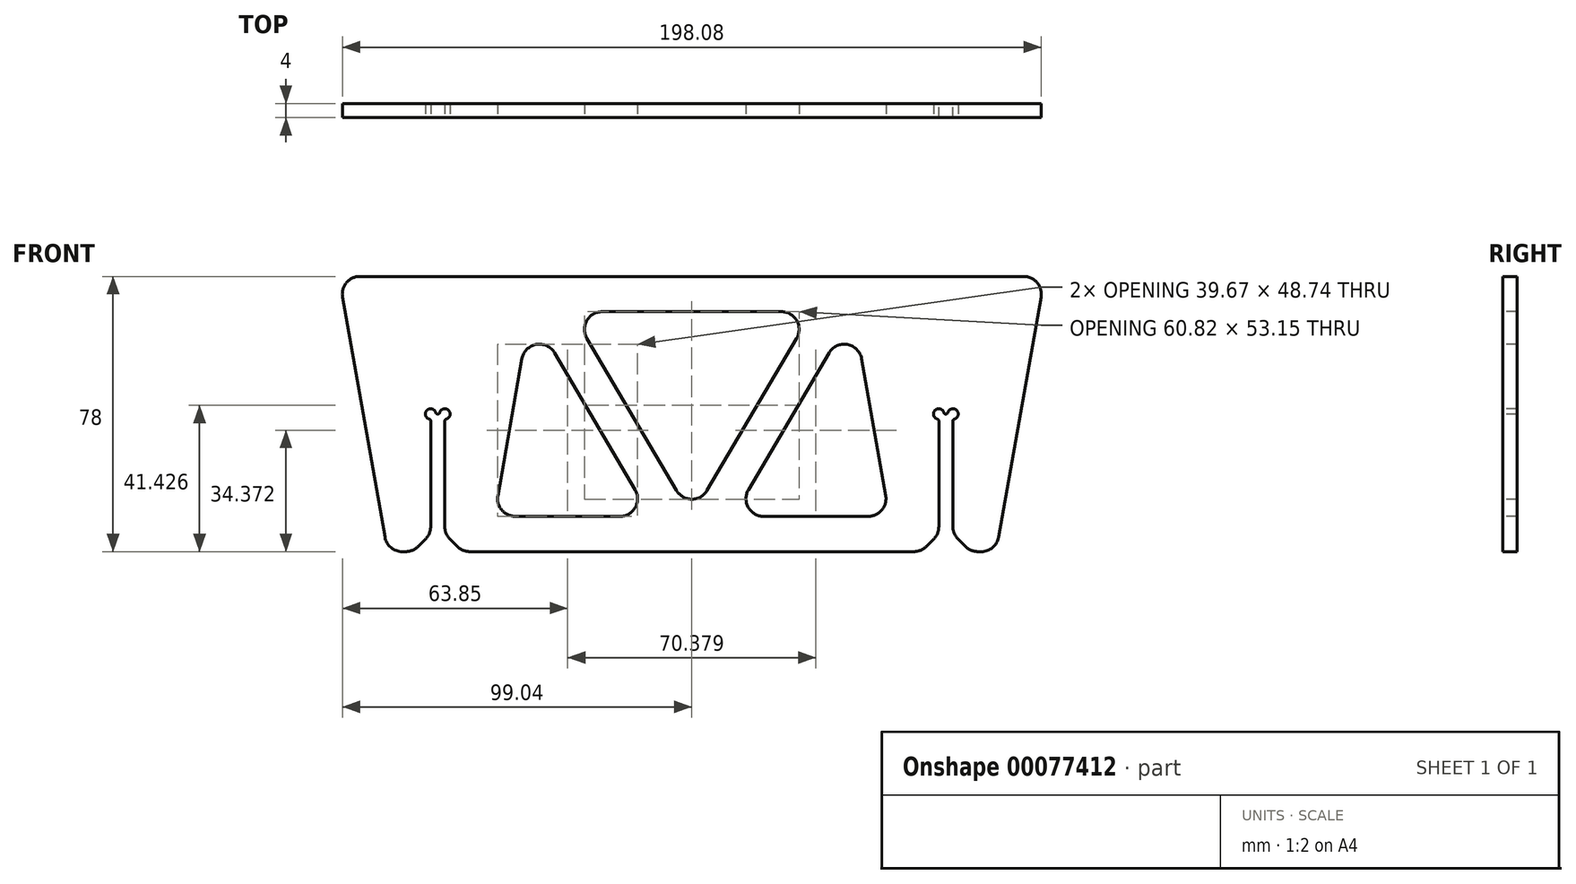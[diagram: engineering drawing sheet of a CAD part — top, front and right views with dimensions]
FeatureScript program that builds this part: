
annotation { "Feature Type Name" : "Feature", "Feature Type Description" : "" }
export const myFeature = defineFeature(function(context is Context, id is Id, definition is map)
    precondition{}
    {
        {
            var Q0;
            Q0=qCreatedBy(makeId("Front.planeOp"),FACE);
            var sketch = newSketch(context, id + "F0", { "sketchPlane" : qUnion([Q0])});
            skLineSegment(sketch, "E0", {"start": v(0, 104.96) * mm, "end": v(0, -105.42) * mm, "construction": true});
            skLineSegment(sketch, "E1", {"start": v(-94.04, 0) * mm, "end": v(94.04, 0) * mm});
            skLineSegment(sketch, "E2", {"start": v(98.97, -5.87) * mm, "end": v(86.98, -73.87) * mm});
            skLineSegment(sketch, "E3", {"start": v(82.05, -78) * mm, "end": v(74, -78) * mm});
            skLineSegment(sketch, "E4", {"start": v(-86.98, -73.87) * mm, "end": v(-98.97, -5.87) * mm});
            skLineSegment(sketch, "E5", {"start": v(-74, -78) * mm, "end": v(-74, -39) * mm});
            skLineSegment(sketch, "E6", {"start": v(-74, -39) * mm, "end": v(-70, -39) * mm});
            skLineSegment(sketch, "E7", {"start": v(-70, -39) * mm, "end": v(-70, -78) * mm});
            skLineSegment(sketch, "E8", {"start": v(74, -78) * mm, "end": v(74, -39) * mm});
            skLineSegment(sketch, "E9", {"start": v(70, -39) * mm, "end": v(74, -39) * mm});
            skLineSegment(sketch, "E10", {"start": v(70, -39) * mm, "end": v(70, -78) * mm});
            skLineSegment(sketch, "E11.trimOffspring", {"start": v(-74, -78) * mm, "end": v(-82.05, -78) * mm});
            skLineSegment(sketch, "E12.trimOffspring", {"start": v(70, -78) * mm, "end": v(-70, -78) * mm});
            skPoint(sketch, "E13.visualSharp", {"position": v(-100, 0) * mm});
            skArc(sketch, "E13.filletArc", {"start": v(-94.04, 0) * mm, "mid": v(-97.87, -1.79) * mm, "end": v(-98.97, -5.87) * mm});
            skPoint(sketch, "E14.visualSharp", {"position": v(-86.25, -78) * mm});
            skArc(sketch, "E14.filletArc", {"start": v(-86.98, -73.87) * mm, "mid": v(-85.26, -76.83) * mm, "end": v(-82.05, -78) * mm});
            skPoint(sketch, "E15.visualSharp", {"position": v(86.25, -78) * mm});
            skArc(sketch, "E15.filletArc", {"start": v(82.05, -78) * mm, "mid": v(85.26, -76.83) * mm, "end": v(86.98, -73.87) * mm});
            skPoint(sketch, "E16.visualSharp", {"position": v(100, 0) * mm});
            skArc(sketch, "E16.filletArc", {"start": v(98.97, -5.87) * mm, "mid": v(97.87, -1.79) * mm, "end": v(94.04, 0) * mm});
            skSolve(sketch);
        }
        {
            var Q0;
            Q0=makeQuery(id+"F0.imprint","IMPRINT",FACE,{"disambiguationData":[TD([[makeQuery(id+"F0.imprint","IMPRINT",EDGE,{"derivedFrom":sQuery(id+"F0.wireOp",EDGE,"E1")}),-1.0]])]});
            extrude(context, id + "F1", {"entities" : qUnion([Q0]), "endBound" : BoundingType.SYMMETRIC, "depth" : 4 * mm});
        }
        {
            var Q0;
            Q0=makeQuery(id+"F1.opExtrude","SWEPT_EDGE",EDGE,{"disambiguationData":[OSD([sQuery(id+"F0.wireOp",EDGE,"E5"),sQuery(id+"F0.wireOp",EDGE,"E11.trimOffspring")])]});
            var Q1;
            Q1=makeQuery(id+"F1.opExtrude","SWEPT_EDGE",EDGE,{"disambiguationData":[OSD([sQuery(id+"F0.wireOp",EDGE,"E7"),sQuery(id+"F0.wireOp",EDGE,"E12.trimOffspring")])]});
            var Q2;
            Q2=makeQuery(id+"F1.opExtrude","SWEPT_EDGE",EDGE,{"disambiguationData":[OSD([sQuery(id+"F0.wireOp",EDGE,"E10"),sQuery(id+"F0.wireOp",EDGE,"E12.trimOffspring")])]});
            var Q3;
            Q3=makeQuery(id+"F1.opExtrude","SWEPT_EDGE",EDGE,{"disambiguationData":[OSD([sQuery(id+"F0.wireOp",EDGE,"E3"),sQuery(id+"F0.wireOp",EDGE,"E8")])]});
            chamfer(context, id + "F2", {"entities" : qUnion([Q0, Q1, Q2, Q3]), "width" : 5 * mm, "tangentPropagation" : true});
        }
        {
            var Q0;
            {var subQ0=sQuery(id+"F0.wireOp",EDGE,"E8");Q0=makeQuery(id+"F2.opChamfer","BLEND_EDGE",EDGE,{"blendedFrom":[makeQuery(id+"F1.opExtrude","SWEPT_EDGE",EDGE,{"disambiguationData":[OSD([sQuery(id+"F0.wireOp",EDGE,"E3"),subQ0])]}),makeQuery(id+"F1.opExtrude","SWEPT_FACE",FACE,{"disambiguationData":[OSD([subQ0])]})],"blendedInto":[makeQuery(id+"F1.opExtrude","SWEPT_FACE",FACE,{"disambiguationData":[OSD([subQ0])]})]});}
            var Q1;
            {var subQ0=sQuery(id+"F0.wireOp",EDGE,"E3");Q1=makeQuery(id+"F2.opChamfer","BLEND_EDGE",EDGE,{"blendedFrom":[makeQuery(id+"F1.opExtrude","SWEPT_EDGE",EDGE,{"disambiguationData":[OSD([subQ0,sQuery(id+"F0.wireOp",EDGE,"E8")])]}),makeQuery(id+"F1.opExtrude","SWEPT_FACE",FACE,{"disambiguationData":[OSD([subQ0])]})],"blendedInto":[makeQuery(id+"F1.opExtrude","SWEPT_FACE",FACE,{"disambiguationData":[OSD([subQ0])]})]});}
            var Q2;
            {var subQ0=sQuery(id+"F0.wireOp",EDGE,"E10");Q2=makeQuery(id+"F2.opChamfer","BLEND_EDGE",EDGE,{"blendedFrom":[makeQuery(id+"F1.opExtrude","SWEPT_EDGE",EDGE,{"disambiguationData":[OSD([subQ0,sQuery(id+"F0.wireOp",EDGE,"E12.trimOffspring")])]}),makeQuery(id+"F1.opExtrude","SWEPT_FACE",FACE,{"disambiguationData":[OSD([subQ0])]})],"blendedInto":[makeQuery(id+"F1.opExtrude","SWEPT_FACE",FACE,{"disambiguationData":[OSD([subQ0])]})]});}
            var Q3;
            {var subQ0=sQuery(id+"F0.wireOp",EDGE,"E12.trimOffspring");Q3=makeQuery(id+"F2.opChamfer","BLEND_EDGE",EDGE,{"blendedFrom":[makeQuery(id+"F1.opExtrude","SWEPT_EDGE",EDGE,{"disambiguationData":[OSD([sQuery(id+"F0.wireOp",EDGE,"E10"),subQ0])]}),makeQuery(id+"F1.opExtrude","SWEPT_FACE",FACE,{"disambiguationData":[OSD([subQ0])]})],"blendedInto":[makeQuery(id+"F1.opExtrude","SWEPT_FACE",FACE,{"disambiguationData":[OSD([subQ0])]})]});}
            var Q4;
            {var subQ0=sQuery(id+"F0.wireOp",EDGE,"E7");Q4=makeQuery(id+"F2.opChamfer","BLEND_EDGE",EDGE,{"blendedFrom":[makeQuery(id+"F1.opExtrude","SWEPT_EDGE",EDGE,{"disambiguationData":[OSD([subQ0,sQuery(id+"F0.wireOp",EDGE,"E12.trimOffspring")])]}),makeQuery(id+"F1.opExtrude","SWEPT_FACE",FACE,{"disambiguationData":[OSD([subQ0])]})],"blendedInto":[makeQuery(id+"F1.opExtrude","SWEPT_FACE",FACE,{"disambiguationData":[OSD([subQ0])]})]});}
            var Q5;
            {var subQ0=sQuery(id+"F0.wireOp",EDGE,"E12.trimOffspring");Q5=makeQuery(id+"F2.opChamfer","BLEND_EDGE",EDGE,{"blendedFrom":[makeQuery(id+"F1.opExtrude","SWEPT_EDGE",EDGE,{"disambiguationData":[OSD([sQuery(id+"F0.wireOp",EDGE,"E7"),subQ0])]}),makeQuery(id+"F1.opExtrude","SWEPT_FACE",FACE,{"disambiguationData":[OSD([subQ0])]})],"blendedInto":[makeQuery(id+"F1.opExtrude","SWEPT_FACE",FACE,{"disambiguationData":[OSD([subQ0])]})]});}
            var Q6;
            {var subQ0=sQuery(id+"F0.wireOp",EDGE,"E5");Q6=makeQuery(id+"F2.opChamfer","BLEND_EDGE",EDGE,{"blendedFrom":[makeQuery(id+"F1.opExtrude","SWEPT_EDGE",EDGE,{"disambiguationData":[OSD([subQ0,sQuery(id+"F0.wireOp",EDGE,"E11.trimOffspring")])]}),makeQuery(id+"F1.opExtrude","SWEPT_FACE",FACE,{"disambiguationData":[OSD([subQ0])]})],"blendedInto":[makeQuery(id+"F1.opExtrude","SWEPT_FACE",FACE,{"disambiguationData":[OSD([subQ0])]})]});}
            var Q7;
            {var subQ0=sQuery(id+"F0.wireOp",EDGE,"E11.trimOffspring");Q7=makeQuery(id+"F2.opChamfer","BLEND_EDGE",EDGE,{"blendedFrom":[makeQuery(id+"F1.opExtrude","SWEPT_EDGE",EDGE,{"disambiguationData":[OSD([sQuery(id+"F0.wireOp",EDGE,"E5"),subQ0])]}),makeQuery(id+"F1.opExtrude","SWEPT_FACE",FACE,{"disambiguationData":[OSD([subQ0])]})],"blendedInto":[makeQuery(id+"F1.opExtrude","SWEPT_FACE",FACE,{"disambiguationData":[OSD([subQ0])]})]});}
            fillet(context, id + "F3", {"entities" : qUnion([Q0, Q1, Q2, Q3, Q4, Q5, Q6, Q7]), "radius" : 5 * mm, "tangentPropagation" : true, "allowEdgeOverflow" : false});
        }
        {
            var Q0;
            Q0=makeQuery(id+"F1.opExtrude","CAP_FACE",FACE,{"disambiguationData":[OSD([sQuery(id+"F0.wireOp",EDGE,"E1"),sQuery(id+"F0.wireOp",EDGE,"E2"),sQuery(id+"F0.wireOp",EDGE,"E3"),sQuery(id+"F0.wireOp",EDGE,"E4"),sQuery(id+"F0.wireOp",EDGE,"E5"),sQuery(id+"F0.wireOp",EDGE,"E6"),sQuery(id+"F0.wireOp",EDGE,"E7"),sQuery(id+"F0.wireOp",EDGE,"E8"),sQuery(id+"F0.wireOp",EDGE,"E9"),sQuery(id+"F0.wireOp",EDGE,"E10"),sQuery(id+"F0.wireOp",EDGE,"E11.trimOffspring"),sQuery(id+"F0.wireOp",EDGE,"E12.trimOffspring"),sQuery(id+"F0.wireOp",EDGE,"E13.filletArc"),sQuery(id+"F0.wireOp",EDGE,"E14.filletArc"),sQuery(id+"F0.wireOp",EDGE,"E15.filletArc"),sQuery(id+"F0.wireOp",EDGE,"E16.filletArc")])],"isStart":false});
            var sketch = newSketch(context, id + "F4", { "sketchPlane" : qUnion([Q0])});
            skCircle(sketch, "E17", {"center": v(74, -39) * mm, "radius": 1.5 * mm});
            skCircle(sketch, "E18", {"center": v(70, -39) * mm, "radius": 1.5 * mm});
            skCircle(sketch, "E19", {"center": v(-70, -39) * mm, "radius": 1.5 * mm});
            skCircle(sketch, "E20", {"center": v(-74, -39) * mm, "radius": 1.5 * mm});
            skSolve(sketch);
        }
        {
            var Q0;
            Q0 = qSketchRegion(id + "F4", true);
            extrude(context, id + "F5", {"entities" : qUnion([Q0]), "operationType" : NewBodyOperationType.REMOVE, "endBound" : BoundingType.THROUGH_ALL, "oppositeDirection" : true, "depth" : 25 * mm});
        }
        {
            var Q0;
            Q0=makeQuery(id+"F5.boolean.opBoolean","INTERSECT",EDGE,{"derivedFrom":[makeQuery(id+"F1.opExtrude","SWEPT_FACE",FACE,{"disambiguationData":[OSD([sQuery(id+"F0.wireOp",EDGE,"E9")])]}),makeQuery(id+"F5.opExtrude","SWEPT_FACE",FACE,{"disambiguationData":[OSD([sQuery(id+"F4.wireOp",EDGE,"E17")])]})]});
            var Q1;
            Q1=makeQuery(id+"F5.boolean.opBoolean","INTERSECT",EDGE,{"derivedFrom":[makeQuery(id+"F1.opExtrude","SWEPT_FACE",FACE,{"disambiguationData":[OSD([sQuery(id+"F0.wireOp",EDGE,"E8")])]}),makeQuery(id+"F5.opExtrude","SWEPT_FACE",FACE,{"disambiguationData":[OSD([sQuery(id+"F4.wireOp",EDGE,"E17")])]})]});
            var Q2;
            Q2=makeQuery(id+"F5.boolean.opBoolean","INTERSECT",EDGE,{"derivedFrom":[makeQuery(id+"F1.opExtrude","SWEPT_FACE",FACE,{"disambiguationData":[OSD([sQuery(id+"F0.wireOp",EDGE,"E9")])]}),makeQuery(id+"F5.opExtrude","SWEPT_FACE",FACE,{"disambiguationData":[OSD([sQuery(id+"F4.wireOp",EDGE,"E18")])]})]});
            var Q3;
            Q3=makeQuery(id+"F5.boolean.opBoolean","INTERSECT",EDGE,{"derivedFrom":[makeQuery(id+"F1.opExtrude","SWEPT_FACE",FACE,{"disambiguationData":[OSD([sQuery(id+"F0.wireOp",EDGE,"E10")])]}),makeQuery(id+"F5.opExtrude","SWEPT_FACE",FACE,{"disambiguationData":[OSD([sQuery(id+"F4.wireOp",EDGE,"E18")])]})]});
            var Q4;
            Q4=makeQuery(id+"F5.boolean.opBoolean","INTERSECT",EDGE,{"derivedFrom":[makeQuery(id+"F1.opExtrude","SWEPT_FACE",FACE,{"disambiguationData":[OSD([sQuery(id+"F0.wireOp",EDGE,"E5")])]}),makeQuery(id+"F5.opExtrude","SWEPT_FACE",FACE,{"disambiguationData":[OSD([sQuery(id+"F4.wireOp",EDGE,"E20")])]})]});
            var Q5;
            Q5=makeQuery(id+"F5.boolean.opBoolean","INTERSECT",EDGE,{"derivedFrom":[makeQuery(id+"F1.opExtrude","SWEPT_FACE",FACE,{"disambiguationData":[OSD([sQuery(id+"F0.wireOp",EDGE,"E6")])]}),makeQuery(id+"F5.opExtrude","SWEPT_FACE",FACE,{"disambiguationData":[OSD([sQuery(id+"F4.wireOp",EDGE,"E20")])]})]});
            var Q6;
            Q6=makeQuery(id+"F5.boolean.opBoolean","INTERSECT",EDGE,{"derivedFrom":[makeQuery(id+"F1.opExtrude","SWEPT_FACE",FACE,{"disambiguationData":[OSD([sQuery(id+"F0.wireOp",EDGE,"E6")])]}),makeQuery(id+"F5.opExtrude","SWEPT_FACE",FACE,{"disambiguationData":[OSD([sQuery(id+"F4.wireOp",EDGE,"E19")])]})]});
            var Q7;
            Q7=makeQuery(id+"F5.boolean.opBoolean","INTERSECT",EDGE,{"derivedFrom":[makeQuery(id+"F1.opExtrude","SWEPT_FACE",FACE,{"disambiguationData":[OSD([sQuery(id+"F0.wireOp",EDGE,"E7")])]}),makeQuery(id+"F5.opExtrude","SWEPT_FACE",FACE,{"disambiguationData":[OSD([sQuery(id+"F4.wireOp",EDGE,"E19")])]})]});
            fillet(context, id + "F6", {"entities" : qUnion([Q0, Q1, Q2, Q3, Q4, Q5, Q6, Q7]), "radius" : 0.5 * mm, "tangentPropagation" : true, "allowEdgeOverflow" : false});
        }
        {
            var Q0;
            Q0=makeQuery(id+"F1.opExtrude","CAP_FACE",FACE,{"disambiguationData":[OSD([sQuery(id+"F0.wireOp",EDGE,"E1"),sQuery(id+"F0.wireOp",EDGE,"E2"),sQuery(id+"F0.wireOp",EDGE,"E3"),sQuery(id+"F0.wireOp",EDGE,"E4"),sQuery(id+"F0.wireOp",EDGE,"E5"),sQuery(id+"F0.wireOp",EDGE,"E6"),sQuery(id+"F0.wireOp",EDGE,"E7"),sQuery(id+"F0.wireOp",EDGE,"E8"),sQuery(id+"F0.wireOp",EDGE,"E9"),sQuery(id+"F0.wireOp",EDGE,"E10"),sQuery(id+"F0.wireOp",EDGE,"E11.trimOffspring"),sQuery(id+"F0.wireOp",EDGE,"E12.trimOffspring"),sQuery(id+"F0.wireOp",EDGE,"E13.filletArc"),sQuery(id+"F0.wireOp",EDGE,"E14.filletArc"),sQuery(id+"F0.wireOp",EDGE,"E15.filletArc"),sQuery(id+"F0.wireOp",EDGE,"E16.filletArc")])],"isStart":false});
            var sketch = newSketch(context, id + "F7", { "sketchPlane" : qUnion([Q0])});
            skLineSegment(sketch, "E21", {"start": v(-72, -80.47) * mm, "end": v(-72, 5.28) * mm, "construction": true});
            skPoint(sketch, "E21.startSnap0", {"position": v(-72, -39) * mm});
            skLineSegment(sketch, "E22", {"start": v(-48.12, -23.35) * mm, "end": v(-54.96, -62.13) * mm});
            skLineSegment(sketch, "E23", {"start": v(-29.72, -17.54) * mm, "end": v(-4.3, -60.68) * mm});
            skLineSegment(sketch, "E24", {"start": v(-38.88, -21.68) * mm, "end": v(-16.04, -60.46) * mm});
            skLineSegment(sketch, "E25", {"start": v(-20.35, -68) * mm, "end": v(-50.03, -68) * mm});
            skLineSegment(sketch, "E26", {"start": v(72, -86.75) * mm, "end": v(72, 4.02) * mm, "construction": true});
            skPoint(sketch, "E26.startSnap0", {"position": v(72, -39) * mm});
            skLineSegment(sketch, "E27", {"start": v(54.96, -62.13) * mm, "end": v(48.12, -23.35) * mm});
            skLineSegment(sketch, "E28", {"start": v(-25.41, -10) * mm, "end": v(25.41, -10) * mm});
            skLineSegment(sketch, "E29", {"start": v(4.3, -60.68) * mm, "end": v(29.72, -17.54) * mm});
            skLineSegment(sketch, "E30", {"start": v(38.88, -21.68) * mm, "end": v(16.04, -60.46) * mm});
            skLineSegment(sketch, "E31", {"start": v(20.35, -68) * mm, "end": v(50.03, -68) * mm});
            skPoint(sketch, "E32.visualSharp", {"position": v(-45.76, -10) * mm});
            skArc(sketch, "E32.filletArc", {"start": v(-38.88, -21.68) * mm, "mid": v(-44.08, -19.3) * mm, "end": v(-48.12, -23.35) * mm});
            skPoint(sketch, "E33.visualSharp", {"position": v(-34.16, -10) * mm});
            skArc(sketch, "E33.filletArc", {"start": v(-25.41, -10) * mm, "mid": v(-29.75, -12.52) * mm, "end": v(-29.72, -17.54) * mm});
            skPoint(sketch, "E34.visualSharp", {"position": v(34.16, -10) * mm});
            skArc(sketch, "E34.filletArc", {"start": v(29.72, -17.54) * mm, "mid": v(29.75, -12.52) * mm, "end": v(25.41, -10) * mm});
            skPoint(sketch, "E35.visualSharp", {"position": v(0, -68) * mm});
            skArc(sketch, "E35.filletArc", {"start": v(-4.3, -60.68) * mm, "mid": v(0, -63.15) * mm, "end": v(4.3, -60.68) * mm});
            skPoint(sketch, "E36.visualSharp", {"position": v(11.6, -68) * mm});
            skArc(sketch, "E36.filletArc", {"start": v(16.04, -60.46) * mm, "mid": v(16.01, -65.48) * mm, "end": v(20.35, -68) * mm});
            skPoint(sketch, "E37.visualSharp", {"position": v(56, -68) * mm});
            skArc(sketch, "E37.filletArc", {"start": v(50.03, -68) * mm, "mid": v(53.86, -66.21) * mm, "end": v(54.96, -62.13) * mm});
            skPoint(sketch, "E38.visualSharp", {"position": v(45.76, -10) * mm});
            skArc(sketch, "E38.filletArc", {"start": v(48.12, -23.35) * mm, "mid": v(44.08, -19.3) * mm, "end": v(38.88, -21.68) * mm});
            skPoint(sketch, "E39.visualSharp", {"position": v(-11.6, -68) * mm});
            skArc(sketch, "E39.filletArc", {"start": v(-20.35, -68) * mm, "mid": v(-16.01, -65.48) * mm, "end": v(-16.04, -60.46) * mm});
            skPoint(sketch, "E40.visualSharp", {"position": v(-56, -68) * mm});
            skArc(sketch, "E40.filletArc", {"start": v(-54.96, -62.13) * mm, "mid": v(-53.86, -66.21) * mm, "end": v(-50.03, -68) * mm});
            skSolve(sketch);
        }
        {
            var Q0;
            Q0=makeQuery(id+"F7.imprint","IMPRINT",FACE,{"disambiguationData":[TD([[makeQuery(id+"F7.imprint","IMPRINT",EDGE,{"derivedFrom":sQuery(id+"F7.wireOp",EDGE,"E22")}),1.0]])]});
            var Q1;
            Q1=makeQuery(id+"F7.imprint","IMPRINT",FACE,{"disambiguationData":[TD([[makeQuery(id+"F7.imprint","IMPRINT",EDGE,{"derivedFrom":sQuery(id+"F7.wireOp",EDGE,"E23")}),1.0]])]});
            var Q2;
            Q2=makeQuery(id+"F7.imprint","IMPRINT",FACE,{"disambiguationData":[TD([[makeQuery(id+"F7.imprint","IMPRINT",EDGE,{"derivedFrom":sQuery(id+"F7.wireOp",EDGE,"E27")}),1.0]])]});
            extrude(context, id + "F8", {"entities" : qUnion([Q0, Q1, Q2]), "operationType" : NewBodyOperationType.REMOVE, "endBound" : BoundingType.THROUGH_ALL, "oppositeDirection" : true, "depth" : 25 * mm});
        }
    });
